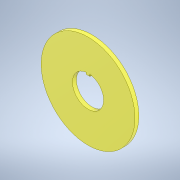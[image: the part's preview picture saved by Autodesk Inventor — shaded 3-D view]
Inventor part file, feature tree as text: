
AUTODESK INVENTOR PART (.ipt)
format: ipt  version: 2021.1 (Build 251245010, 245A)  size: 125,952 bytes
history: native  units: in
note: dims shown in document units (in); Inventor stores cm internally (conversion verified against a paired STEP export)
features: extrude x4, sketch x4, pattern_circular x1
ambient origin geometry x8: Origin, YZ Plane, XZ Plane, XY Plane, X Axis, Y Axis, Z Axis, Center Point
bodies: Solid1 (feature_tree)
feature tree (9):
  extrude  "Extrusion1"  Depth=0.25in TaperAngle=0.0deg
  extrude  "Extrusion3"  TaperAngle=0.0deg  [1 undecoded]
  extrude  "Extrusion4"  Depth=0.25in
  pattern_circular  "Circular Pattern1"  Count=6 Angle=360.0deg
  extrude  "Extrusion5"  Depth=3.0in
  sketch  "Sketch1"  dims[d0=6.0in d1=0.25in d2=0.0in]
  sketch  "Sketch3"  dims[d8=2.0in d9=0.0in d10=0.0in]
  sketch  "Sketch5"  dims[d11=0.125in d13=0.25in]
  sketch  "Sketch7"  dims[d14=0.25in d15=0.0in d16=2.3622in d17=360.0deg d19=3.0in d20=0.375in d21=0.25in d22=0.0in]
note: 1 required parameter value undecoded (feature->parameter linkage not recoverable at this tier; creation-order binding heuristic only, values carry confidence <= 0.55)
